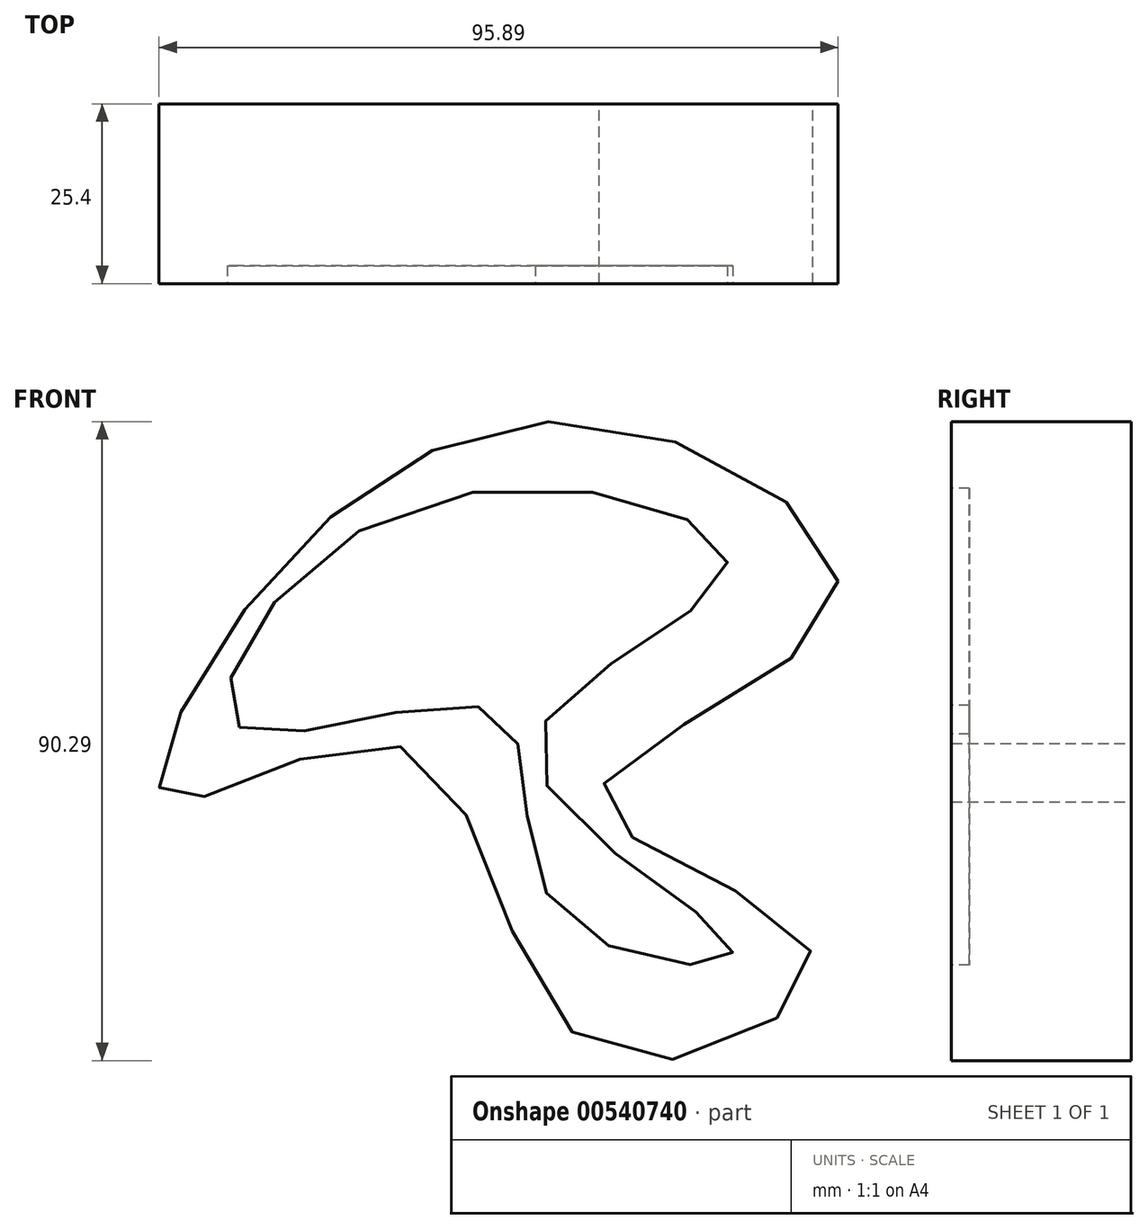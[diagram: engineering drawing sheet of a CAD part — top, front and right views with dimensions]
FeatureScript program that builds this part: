
annotation { "Feature Type Name" : "Feature", "Feature Type Description" : "" }
export const myFeature = defineFeature(function(context is Context, id is Id, definition is map)
    precondition{}
    {
        {
            var Q0;
            Q0=qCreatedBy(makeId("Front.planeOp"),FACE);
            var sketch = newSketch(context, id + "F0", { "sketchPlane" : qUnion([Q0])});
            skFitSpline(sketch, "E0", {"points": [v(-50.02, 0) * mm, v(0, 26.26) * mm, v(33.07, 0) * mm, v(0, -27.03) * mm, v(30.06, -49) * mm, v(0, -62.25) * mm, v(-26.84, -19.8) * mm, v(-60.55, -27.03) * mm, v(-50.02, 0) * mm]});
            skSolve(sketch);
        }
        {
            var Q0;
            Q0 = qSketchRegion(id + "F0", true);
            extrude(context, id + "F1", {"entities" : qUnion([Q0]), "depth" : 25.4 * mm, "offsetDistance" : 25.4 * mm});
        }
        {
            var Q0;
            Q0=makeQuery(id+"F1.opExtrude","CAP_FACE",FACE,{"disambiguationData":[OSD([sQuery(id+"F0.wireOp",EDGE,"E0")])],"isStart":false});
            var sketch = newSketch(context, id + "F2", { "sketchPlane" : qUnion([Q0])});
            skFitSpline(sketch, "E1", {"points": [v(-50.8, -16.59) * mm, v(-28, 13.97) * mm, v(18.01, 5.7) * mm, v(-9.04, -20.26) * mm, v(18.85, -48.25) * mm, v(-5.63, -42.72) * mm, v(-14.66, -14.55) * mm, v(-50.8, -16.59) * mm]});
            skSolve(sketch);
        }
        {
            var Q0;
            Q0 = qSketchRegion(id + "F2", true);
            extrude(context, id + "F3", {"entities" : qUnion([Q0]), "operationType" : NewBodyOperationType.REMOVE, "oppositeDirection" : true, "depth" : 2.54 * mm, "offsetDistance" : 25.4 * mm});
        }
    });
